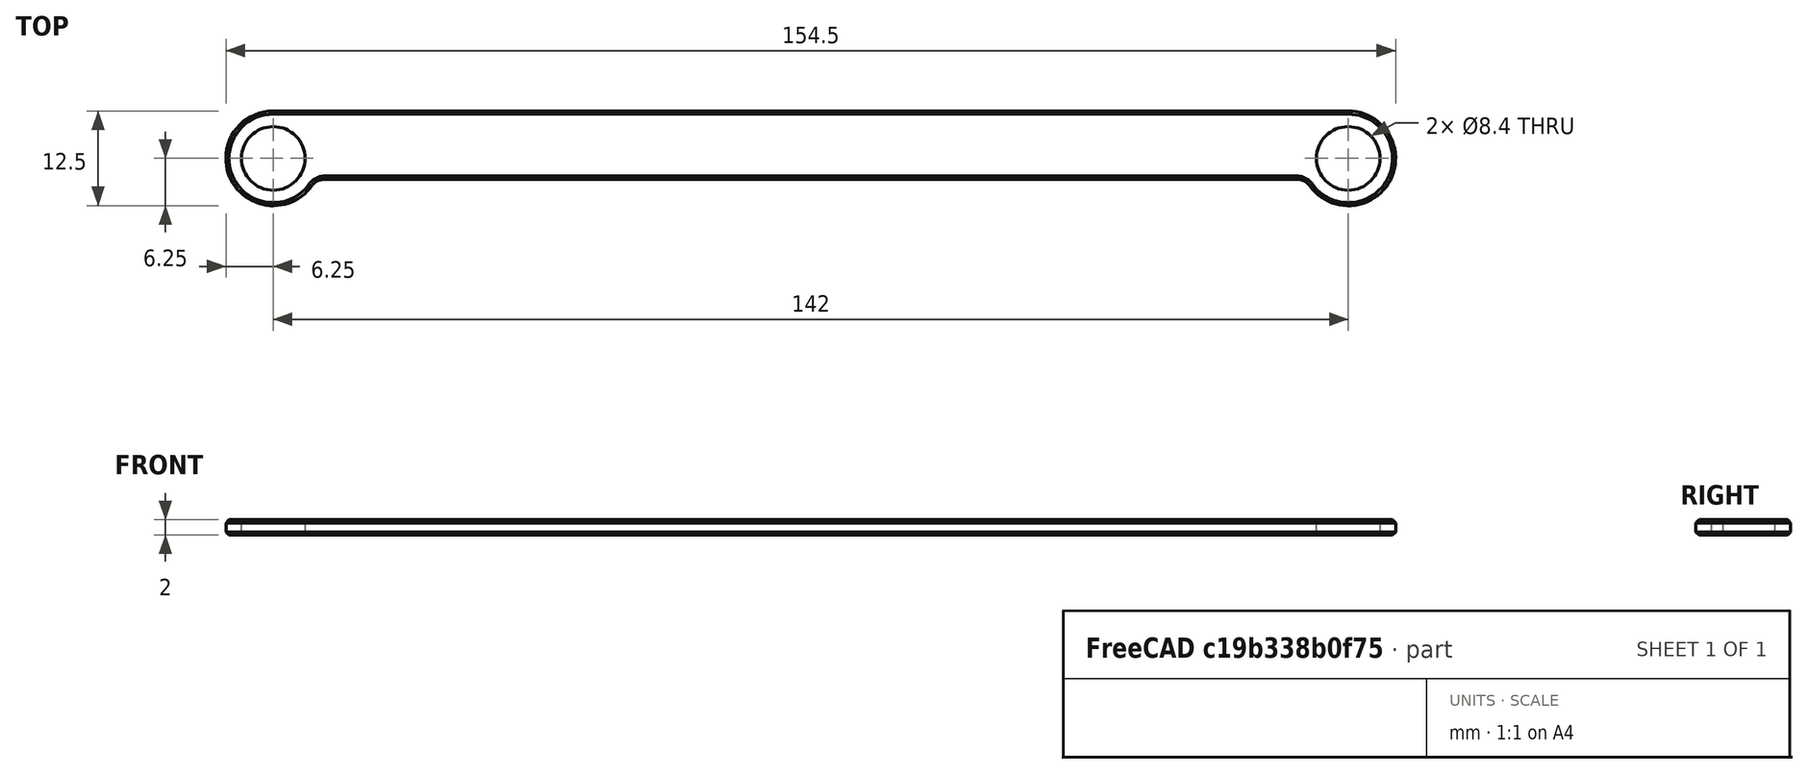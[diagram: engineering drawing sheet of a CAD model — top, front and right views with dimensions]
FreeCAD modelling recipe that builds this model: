
FCSTD DOCUMENT  (FreeCAD 0.18R16146 (Git))
Label: ResizedRightChainAuxiliaryRod
License: All rights reserved
LicenseURL: http://en.wikipedia.org/wiki/All_rights_reserved
objects: Part::Feature×1, PartDesign::FeatureBase×1, Sketcher::SketchObject×1, PartDesign::Pocket×1, PartDesign::Body×1
note: 6 computed .brp shape members not serialized (recipe doc carries the construction recipe); baked Part::Feature solids carry a one-line shape summary decoded from their .brp

FEATURE [Part::Feature] Part__Feature010  label="Ԓ²ၬ¸ɀ"
  Placement = pos=(135.498,217.539,-134.404) rot=(0,0,-1;1.85586rad)
  shape: bbox 52.43 x 148.8 x 2 mm, 27 faces (baked)
FEATURE [PartDesign::FeatureBase] BaseFeature
  BaseFeature = -> Part__Feature010
FEATURE [Sketcher::SketchObject] Sketch
  ExternalGeometry = -> [BaseFeature]
  MapMode = 5
  Placement = pos=(0,0,1) rot=(0,0,1;0rad)
  Support = -> [BaseFeature]
  sketch-geometry (2):
    g0: Circle CenterX=-71 CenterY=0 CenterZ=0 NormalX=0 NormalY=0 NormalZ=1 AngleXU=0 Radius=4.2
    g1: Circle CenterX=71 CenterY=0 CenterZ=0 NormalX=0 NormalY=0 NormalZ=1 AngleXU=0 Radius=4.2
  constraints (4):
    c: Radius(g0) = 4.2
    c: Coincident(g-4,g0)
    c: Coincident(g1,g-6)
    c: Radius(g1) = 4.2
FEATURE [PartDesign::Pocket] Pocket
  BaseFeature = -> BaseFeature
  Length = 5
  Length2 = 100
  Profile = -> Sketch
  Type = 1
FEATURE [PartDesign::Body] Body
  BaseFeature = -> Part__Feature010
  Group = -> [BaseFeature,Sketch,Pocket]
  Origin = -> Origin
  Tip = -> Pocket
